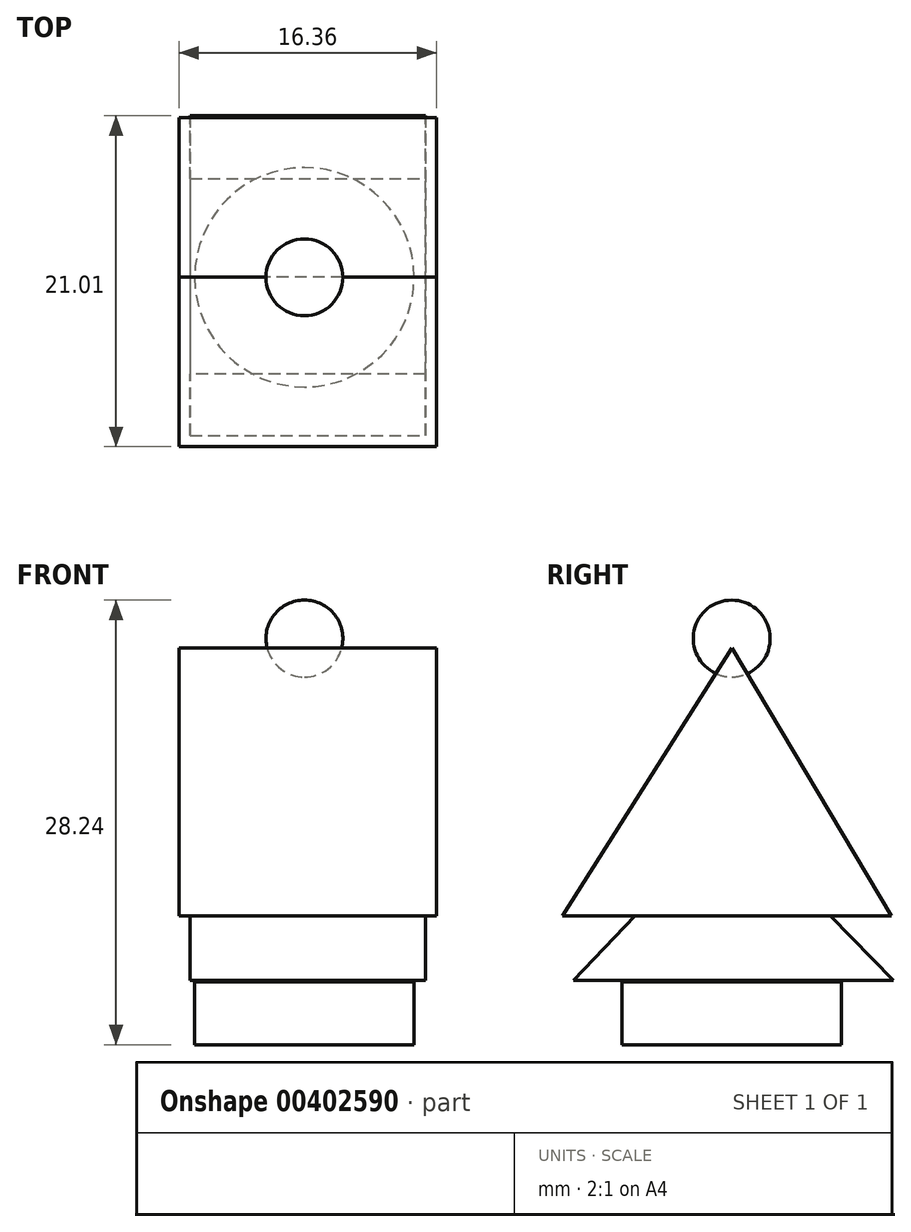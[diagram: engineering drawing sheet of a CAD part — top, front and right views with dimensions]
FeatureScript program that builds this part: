
annotation { "Feature Type Name" : "Feature", "Feature Type Description" : "" }
export const myFeature = defineFeature(function(context is Context, id is Id, definition is map)
    precondition{}
    {
        {
            var Q0;
            Q0=qCreatedBy(makeId("Top.planeOp"),FACE);
            var sketch = newSketch(context, id + "F0", { "sketchPlane" : qUnion([Q0])});
            skCircle(sketch, "E0", {"center": v(0, 0) * mm, "radius": 12.44 * mm});
            skSolve(sketch);
        }
        {
            var Q0;
            Q0=makeQuery(id+"F0.imprint","IMPRINT",FACE,{"disambiguationData":[TD([[makeQuery(id+"F0.imprint","IMPRINT",EDGE,{"derivedFrom":sQuery(id+"F0.wireOp",EDGE,"E0")}),1.0]])]});
            extrude(context, id + "F1", {"entities" : qUnion([Q0]), "depth" : 7.11 * mm});
        }
        {
            var Q0;
            Q0=qCreatedBy(makeId("Right.planeOp"),FACE);
            var sketch = newSketch(context, id + "F2", { "sketchPlane" : qUnion([Q0])});
            skLineSegment(sketch, "E1", {"start": v(18.33, 7.3) * mm, "end": v(-17.93, 7.3) * mm});
            skLineSegment(sketch, "E2", {"start": v(-17.93, 7.3) * mm, "end": v(0, 26.01) * mm});
            skLineSegment(sketch, "E3", {"start": v(0, 26.01) * mm, "end": v(18.33, 7.3) * mm});
            skSolve(sketch);
        }
        {
            var Q0;
            Q0=makeQuery(id+"F2.imprint","IMPRINT",FACE,{"disambiguationData":[TD([[makeQuery(id+"F2.imprint","IMPRINT",EDGE,{"derivedFrom":sQuery(id+"F2.wireOp",EDGE,"E1")}),-1.0]])]});
            extrude(context, id + "F3", {"entities" : qUnion([Q0]), "oppositeDirection" : true, "depth" : 12.95 * mm});
        }
        {
            var Q0;
            Q0 = qSketchRegion(id + "F2", true);
            extrude(context, id + "F4", {"entities" : qUnion([Q0]), "operationType" : NewBodyOperationType.ADD, "depth" : 13.72 * mm});
        }
        {
            var Q0;
            Q0=qCreatedBy(makeId("Right.planeOp"),FACE);
            var sketch = newSketch(context, id + "F5", { "sketchPlane" : qUnion([Q0])});
            skLineSegment(sketch, "E4", {"start": v(18.13, 14.58) * mm, "end": v(-16.97, 14.58) * mm});
            skLineSegment(sketch, "E5", {"start": v(0, 44.97) * mm, "end": v(18.13, 14.58) * mm});
            skLineSegment(sketch, "E6", {"start": v(-16.97, 14.58) * mm, "end": v(-19.2, 14.58) * mm});
            skLineSegment(sketch, "E7", {"start": v(-19.2, 14.58) * mm, "end": v(0, 44.97) * mm});
            skSolve(sketch);
        }
        {
            var Q0;
            Q0=makeQuery(id+"F5.imprint","IMPRINT",FACE,{"disambiguationData":[TD([[makeQuery(id+"F5.imprint","IMPRINT",EDGE,{"derivedFrom":sQuery(id+"F5.wireOp",EDGE,"E4")}),-1.0]])]});
            extrude(context, id + "F6", {"entities" : qUnion([Q0]), "operationType" : NewBodyOperationType.ADD, "depth" : 15 * mm});
        }
        {
            var Q0;
            Q0=makeQuery(id+"F6.opExtrude","CAP_FACE",FACE,{"disambiguationData":[OSD([sQuery(id+"F5.wireOp",EDGE,"E4"),sQuery(id+"F5.wireOp",EDGE,"E5"),sQuery(id+"F5.wireOp",EDGE,"E6"),sQuery(id+"F5.wireOp",EDGE,"E7")])],"isStart":false});
            extrude(context, id + "F7", {"entities" : qUnion([Q0]), "operationType" : NewBodyOperationType.ADD, "oppositeDirection" : true, "depth" : 29.2 * mm});
        }
        {
            var Q0;
            Q0=makeQuery(id+"F3.opExtrude","SWEPT_BODY",BODY,{"disambiguationData":[OSD([sQuery(id+"F2.wireOp",EDGE,"E1"),sQuery(id+"F2.wireOp",EDGE,"E2"),sQuery(id+"F2.wireOp",EDGE,"E3")])]});
            var Q1;
            Q1=makeQuery(id+"F1.opExtrude","SWEPT_BODY",BODY,{"disambiguationData":[OSD([sQuery(id+"F0.wireOp",EDGE,"E0")])]});
            var Q2;
            Q2=qCreatedBy(makeId("Origin.pointOp"),VERTEX);
            transform(context, id + "F8", {"entities" : qUnion([Q0, Q1]), "transformType" : TransformType.SCALE_UNIFORMLY, "scale" : 0.8, "scalePoint" : qUnion([Q2]), "makeCopy" : false});
        }
        {
            var Q0;
            Q0=qCreatedBy(makeId("Right.planeOp"),FACE);
            var sketch = newSketch(context, id + "F9", { "sketchPlane" : qUnion([Q0])});
            skCircle(sketch, "E8", {"center": v(0, 36.85) * mm, "radius": 3.49 * mm});
            skLineSegment(sketch, "E9", {"start": v(0, 33.37) * mm, "end": v(0, 40.34) * mm});
            skSolve(sketch);
        }
        {
            var Q0;
            {var subQ0=sQuery(id+"F9.wireOp",EDGE,"E9");Q0=makeQuery(id+"F9.imprint","IMPRINT",FACE,{"disambiguationData":[TD([[makeQuery(id+"F9.imprint","IMPRINT",EDGE,{"derivedFrom":subQ0}),-1.0]])]});}
            var Q1;
            Q1=sQuery(id+"F9.wireOp",EDGE,"E9");
            revolve(context, id + "F10", {"entities" : qUnion([Q0]), "axis" : qUnion([Q1]), "revolveType" : RevolveType.FULL});
        }
        {
            var Q0;
            Q0=makeQuery(id+"F1.opExtrude","SWEPT_BODY",BODY,{"disambiguationData":[OSD([sQuery(id+"F0.wireOp",EDGE,"E0")])]});
            var Q1;
            Q1=makeQuery(id+"F3.opExtrude","SWEPT_BODY",BODY,{"disambiguationData":[OSD([sQuery(id+"F2.wireOp",EDGE,"E1"),sQuery(id+"F2.wireOp",EDGE,"E2"),sQuery(id+"F2.wireOp",EDGE,"E3")])]});
            var Q2;
            Q2=makeQuery(id+"F10.opRevolve","SWEPT_BODY",BODY,{"disambiguationData":[OSD([sQuery(id+"F9.wireOp",EDGE,"E8"),sQuery(id+"F9.wireOp",EDGE,"E9")])]});
            var Q3;
            Q3=qCreatedBy(makeId("Origin.pointOp"),VERTEX);
            transform(context, id + "F11", {"entities" : qUnion([Q0, Q1, Q2]), "transformType" : TransformType.SCALE_UNIFORMLY, "scale" : 0.7, "scalePoint" : qUnion([Q3]), "makeCopy" : false});
        }
    });
